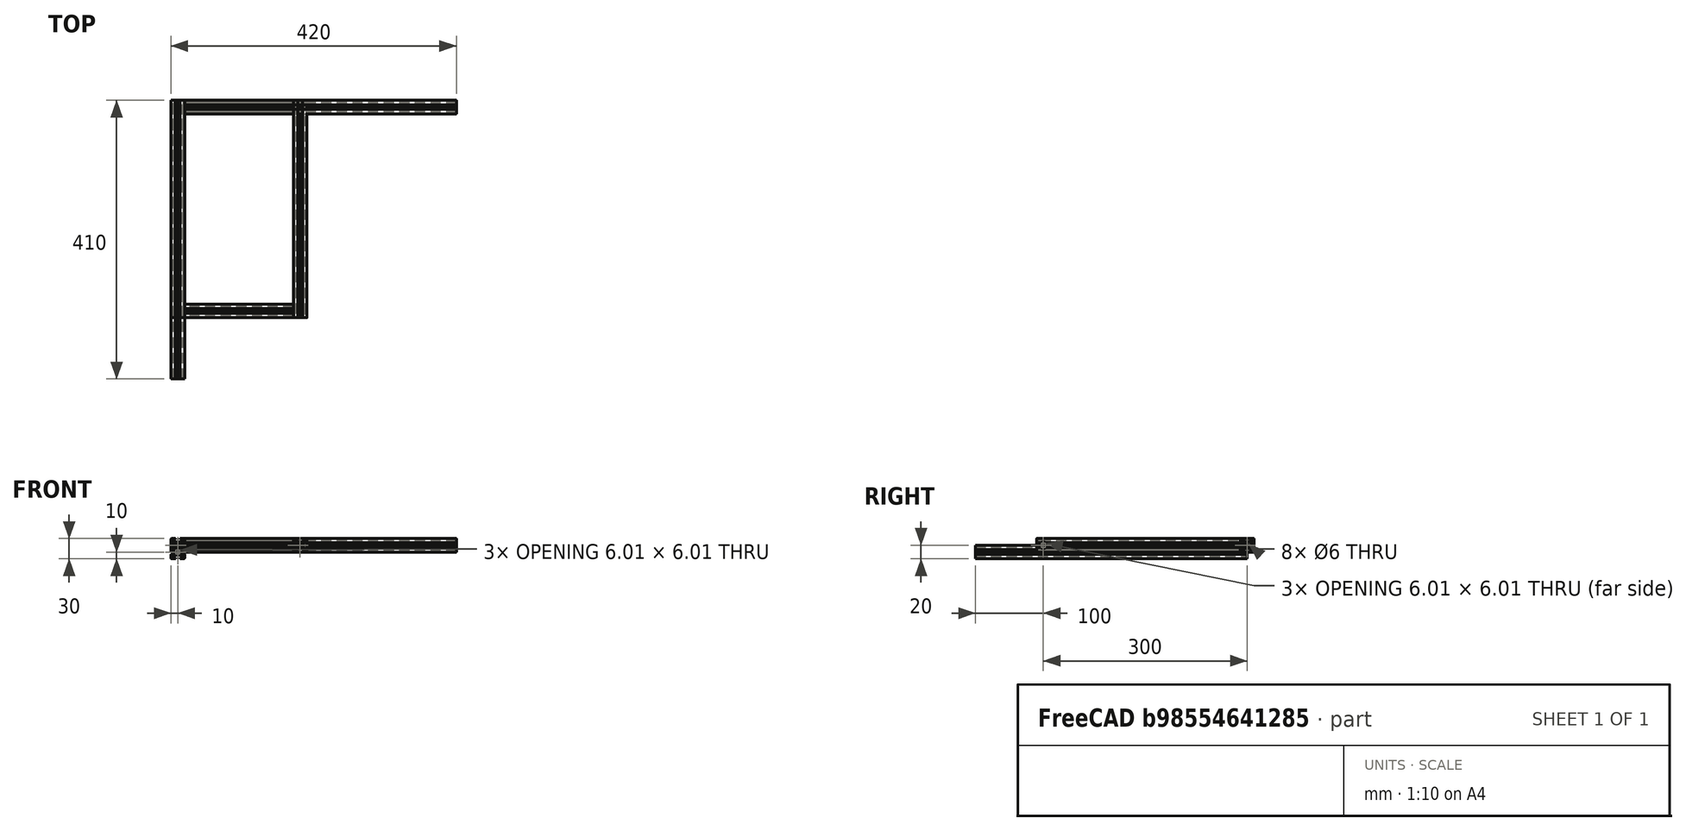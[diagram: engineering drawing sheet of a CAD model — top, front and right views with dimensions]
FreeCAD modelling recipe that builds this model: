
FCSTD DOCUMENT  (FreeCAD 0.17R9796 (Git))
Label: UPKframe2c
License: All rights reserved
LicenseURL: http://en.wikipedia.org/wiki/All_rights_reserved
objects: Part::Feature×6, Part::FeaturePython×4, App::Part×1
note: 10 computed .brp shape members not serialized (recipe doc carries the construction recipe); baked Part::Feature solids carry a one-line shape summary decoded from their .brp

FEATURE [Part::Feature] Pocket001001  label="tslot40"
  Placement = pos=(0,0,0) rot=(1,0,0;1.5708rad)
  shape: bbox 20 x 400 x 20 mm, 94 faces (baked)
FEATURE [Part::Feature] Pocket003001  label="tslot32con"
  Placement = pos=(0,10,10) rot=(1,0,0;1.5708rad)
  shape: bbox 20 x 320 x 20 mm, 150 faces (baked)
FEATURE [Part::Feature] Pocket003002  label="tslot16"
  Placement = pos=(10,0,10) rot=(0,1,0;1.5708rad)
  shape: bbox 160 x 20 x 20 mm, 94 faces (baked)
FEATURE [Part::Feature] Pocket003005  label="tslot40__001"
  Placement = pos=(10,0,10) rot=(0.57735,0.57735,0.57735;2.0944rad)
  shape: bbox 400 x 20 x 20 mm, 94 faces (baked)
FEATURE [Part::Feature] Pocket003006  label="tslot16_001"
  Placement = pos=(10,-300,10) rot=(0,1,0;1.5708rad)
  shape: bbox 160 x 20 x 20 mm, 94 faces (baked)
FEATURE [Part::Feature] Pocket003007  label="tslot32con_001"
  Placement = pos=(180,-310,10) rot=(0,0.707107,0.707107;3.14159rad)
  shape: bbox 20 x 320 x 20 mm, 150 faces (baked)
FEATURE [Part::FeaturePython] Screw  label="M6x25-Screw"  # Fasteners workbench fastener (typed FeaturePython)
  Placement = pos=(-4,0,10) rot=(0,1,0;4.71239rad)
  diameter = 7
  invert = false
  length = 6
  matchOuter = false
  offset = 0
  thread = false
  type = 15
FEATURE [Part::FeaturePython] Screw001  label="M6x25-Screw004"  # Fasteners workbench fastener (typed FeaturePython)
  Placement = pos=(-4,-300,10) rot=(0,-1,0;1.5708rad)
  diameter = 7
  invert = false
  length = 6
  matchOuter = false
  offset = 0
  thread = false
  type = 15
FEATURE [Part::FeaturePython] Screw002  label="M6x25-Screw005"  # Fasteners workbench fastener (typed FeaturePython)
  Placement = pos=(184,0,10) rot=(0,1,0;1.5708rad)
  diameter = 7
  invert = false
  length = 6
  matchOuter = false
  offset = 0
  thread = false
  type = 15
FEATURE [Part::FeaturePython] Screw004  label="M6x25-Screw006"  # Fasteners workbench fastener (typed FeaturePython)
  Placement = pos=(184,-300,10) rot=(0,1,0;1.5708rad)
  diameter = 7
  invert = false
  length = 6
  matchOuter = false
  offset = 0
  thread = false
  type = 15
FEATURE [App::Part] Part  label="lower_frame"
  Group = -> [Pocket003001,Pocket003002,Pocket003006,Pocket003007,Screw,Screw001,Screw002,Screw004]
  License = CC BY 3.0
  LicenseURL = http://creativecommons.org/licenses/by/3.0/
  Origin = -> PartOrigin
